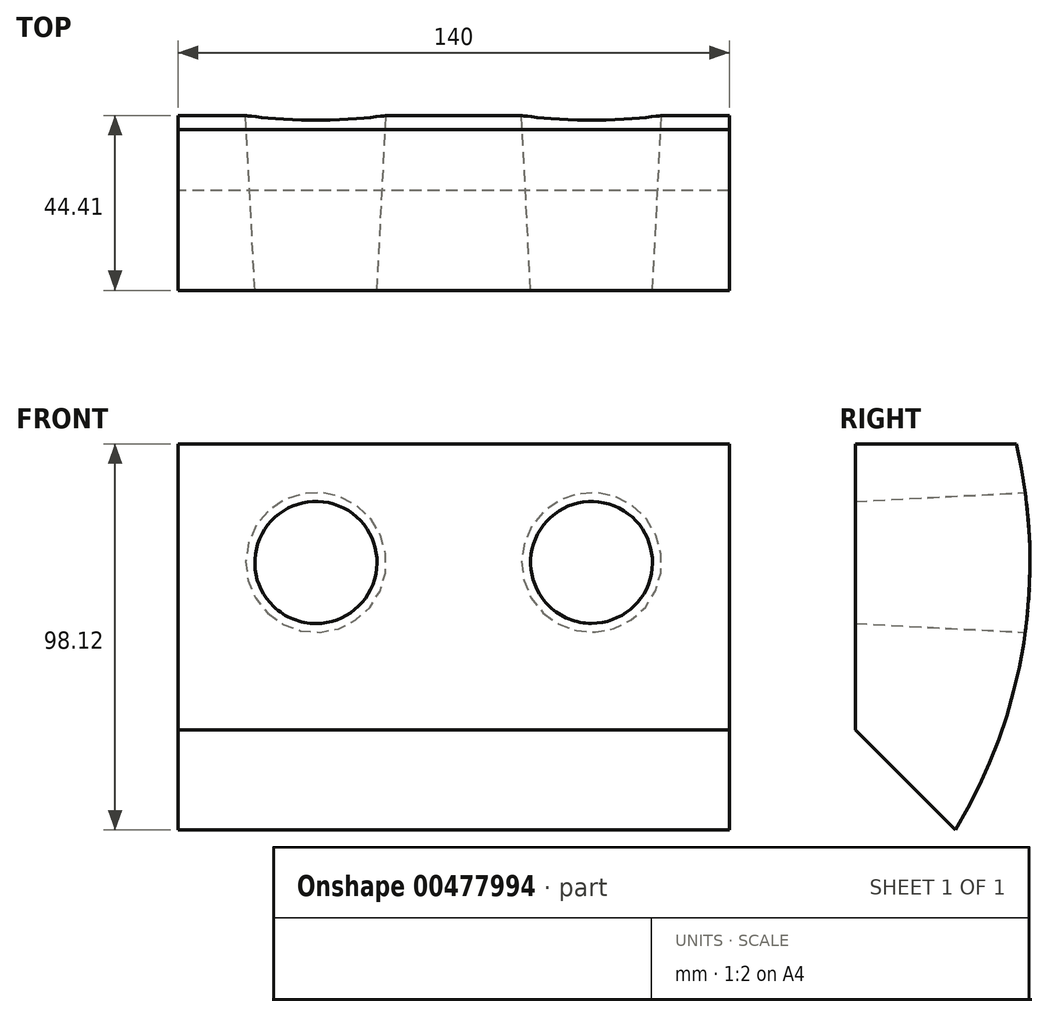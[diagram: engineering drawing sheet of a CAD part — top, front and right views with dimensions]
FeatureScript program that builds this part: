
annotation { "Feature Type Name" : "Feature", "Feature Type Description" : "" }
export const myFeature = defineFeature(function(context is Context, id is Id, definition is map)
    precondition{}
    {
        {
            var Q0;
            Q0=qCreatedBy(makeId("Right.planeOp"),FACE);
            cPlane(context, id + "F0", {"entities" : qUnion([Q0]), "cplaneType" : CPlaneType.OFFSET, "offset" : 70 * mm, "oppositeDirection" : true, "width" : 152.4 * mm, "height" : 152.4 * mm});
        }
        {
            var Q0;
            Q0=qCreatedBy(id+"F0.planeOp",FACE);
            var sketch = newSketch(context, id + "F1", { "sketchPlane" : qUnion([Q0])});
            skLineSegment(sketch, "E0", {"start": v(0, 0) * mm, "end": v(19.01, 0) * mm});
            skLineSegment(sketch, "E1", {"start": v(0, 0) * mm, "end": v(0, 67.98) * mm});
            skLineSegment(sketch, "E2", {"start": v(0, 0) * mm, "end": v(0, -67.97) * mm});
            skArc(sketch, "E3", {"start": v(0, -67.97) * mm, "mid": v(19.01, 0) * mm, "end": v(0, 67.98) * mm});
            skSolve(sketch);
        }
        {
            var Q0;
            {var subQ0=sQuery(id+"F1.wireOp",EDGE,"E0");Q0=makeQuery(id+"F1.imprint","IMPRINT",FACE,{"disambiguationData":[TD([[makeQuery(id+"F1.imprint","IMPRINT",EDGE,{"derivedFrom":subQ0}),1.0]])]});}
            var Q1;
            {var subQ0=sQuery(id+"F1.wireOp",EDGE,"E0");Q1=makeQuery(id+"F1.imprint","IMPRINT",FACE,{"disambiguationData":[TD([[makeQuery(id+"F1.imprint","IMPRINT",EDGE,{"derivedFrom":subQ0}),-1.0]])]});}
            var Q2;
            Q2 = qSketchRegion(id + "F1", true);
            extrude(context, id + "F2", {"entities" : qUnion([Q0, Q1, Q2]), "depth" : 140 * mm});
        }
        {
            var Q0;
            Q0=makeQuery(id+"F2.opExtrude","SWEPT_FACE",FACE,{"disambiguationData":[OSD([sQuery(id+"F1.wireOp",EDGE,"E1"),sQuery(id+"F1.wireOp",EDGE,"E2")])]});
            extrude(context, id + "F3", {"entities" : qUnion([Q0]), "operationType" : NewBodyOperationType.ADD, "depth" : 25.4 * mm});
        }
        {
            var Q0;
            Q0=makeQuery(id+"F3.opExtrude","CAP_FACE",FACE,{"disambiguationData":[OSD([sQuery(id+"F1.wireOp",EDGE,"E1"),sQuery(id+"F1.wireOp",EDGE,"E2")])],"isStart":false});
            var sketch = newSketch(context, id + "F4", { "sketchPlane" : qUnion([Q0])});
            skLineSegment(sketch, "E4", {"start": v(0, 0) * mm, "end": v(-35.01, 0) * mm});
            skLineSegment(sketch, "E5", {"start": v(0, 0) * mm, "end": v(35.01, 0) * mm});
            skSolve(sketch);
        }
        {
            var Q0;
            {var subQ0=sQuery(id+"F1.wireOp",EDGE,"E3");var subQ1=sQuery(id+"F1.wireOp",EDGE,"E1");Q0=makeQuery(id+"F4.imprint","IMPRINT",FACE,{"disambiguationData":[TD([[makeQuery(id+"F4.imprint","IMPRINT",EDGE,{"derivedFrom":makeQuery(id+"F3.opExtrude","CAP_EDGE",EDGE,{"disambiguationData":[OSD([subQ1,subQ0])],"isStart":false})}),1.0]])]});}
            var sketch = newSketch(context, id + "F5", { "sketchPlane" : qUnion([Q0])});
            skCircle(sketch, "E6", {"center": v(-35.02, 0) * mm, "radius": 15.52 * mm});
            skCircle(sketch, "E7", {"center": v(35, 0) * mm, "radius": 15.48 * mm});
            skLineSegment(sketch, "E8.bottom", {"start": v(-19.32, -15.87) * mm, "end": v(-50.71, -15.87) * mm});
            skLineSegment(sketch, "E8.top", {"start": v(-19.32, 15.87) * mm, "end": v(-50.71, 15.87) * mm});
            skLineSegment(sketch, "E8.left", {"start": v(-19.32, -15.87) * mm, "end": v(-19.32, 15.87) * mm});
            skLineSegment(sketch, "E8.right", {"start": v(-50.71, -15.87) * mm, "end": v(-50.71, 15.87) * mm});
            skLineSegment(sketch, "E9.bottom", {"start": v(50.7, -15.87) * mm, "end": v(19.32, -15.87) * mm});
            skLineSegment(sketch, "E9.top", {"start": v(50.7, 15.87) * mm, "end": v(19.32, 15.87) * mm});
            skLineSegment(sketch, "E9.left", {"start": v(50.7, -15.87) * mm, "end": v(50.7, 15.87) * mm});
            skLineSegment(sketch, "E9.right", {"start": v(19.32, -15.87) * mm, "end": v(19.32, 15.87) * mm});
            skSolve(sketch);
        }
        {
            var Q0;
            Q0=qCreatedBy(id+"F0.planeOp",FACE);
            var sketch = newSketch(context, id + "F6", { "sketchPlane" : qUnion([Q0])});
            skLineSegment(sketch, "E10.bottom", {"start": v(-80.1, 30.15) * mm, "end": v(135.05, 30.15) * mm});
            skLineSegment(sketch, "E10.top", {"start": v(-80.1, 114.47) * mm, "end": v(135.05, 114.47) * mm});
            skLineSegment(sketch, "E10.left", {"start": v(-80.1, 30.15) * mm, "end": v(-80.1, 114.47) * mm});
            skLineSegment(sketch, "E10.right", {"start": v(135.05, 30.15) * mm, "end": v(135.05, 114.47) * mm});
            skPoint(sketch, "E10.middle", {"position": v(27.47, 72.31) * mm});
            skSolve(sketch);
        }
        {
            var Q0;
            Q0=makeQuery(id+"F6.imprint","IMPRINT",FACE,{"disambiguationData":[TD([[makeQuery(id+"F6.imprint","IMPRINT",EDGE,{"derivedFrom":sQuery(id+"F6.wireOp",EDGE,"E10.bottom")}),1.0]])]});
            extrude(context, id + "F7", {"entities" : qUnion([Q0]), "operationType" : NewBodyOperationType.REMOVE, "endBound" : BoundingType.THROUGH_ALL, "depth" : 25.4 * mm});
        }
        {
            var Q0;
            {var subQ0=sQuery(id+"F1.wireOp",EDGE,"E2");var subQ1=sQuery(id+"F1.wireOp",EDGE,"E1");Q0=makeQuery(id+"F3.boolean.opBoolean","MERGE",FACE,{"derivedFrom":[makeQuery(id+"F2.opExtrude","CAP_FACE",FACE,{"disambiguationData":[OSD([subQ1,subQ0,sQuery(id+"F1.wireOp",EDGE,"E3")])],"isStart":true}),makeQuery(id+"F3.opExtrude","SWEPT_FACE",FACE,{"disambiguationData":[OSD([subQ1,subQ0]),TDD([makeQuery(id+"F2.opExtrude","CAP_EDGE",EDGE,{"disambiguationData":[OSD([subQ1,subQ0])],"isStart":true})])]})]});}
            var sketch = newSketch(context, id + "F8", { "sketchPlane" : qUnion([Q0])});
            skLineSegment(sketch, "E11", {"start": v(25.4, -67.97) * mm, "end": v(25.4, -42.57) * mm});
            skLineSegment(sketch, "E12", {"start": v(25.4, -42.57) * mm, "end": v(0, -67.97) * mm});
            skLineSegment(sketch, "E13", {"start": v(0, -67.97) * mm, "end": v(25.4, -67.97) * mm});
            skSolve(sketch);
        }
        {
            var Q0;
            Q0=makeQuery(id+"F8.imprint","IMPRINT",FACE,{"disambiguationData":[TD([[makeQuery(id+"F8.imprint","IMPRINT",EDGE,{"derivedFrom":sQuery(id+"F8.wireOp",EDGE,"E11")}),1.0]])]});
            extrude(context, id + "F9", {"entities" : qUnion([Q0]), "operationType" : NewBodyOperationType.REMOVE, "endBound" : BoundingType.THROUGH_ALL, "oppositeDirection" : true, "depth" : 25.4 * mm});
        }
        {
            var Q0;
            Q0=makeQuery(id+"F5.imprint","IMPRINT",FACE,{"disambiguationData":[TD([[makeQuery(id+"F5.imprint","IMPRINT",EDGE,{"derivedFrom":sQuery(id+"F5.wireOp",EDGE,"E6")}),1.0]])]});
            var Q1;
            Q1=makeQuery(id+"F5.imprint","IMPRINT",FACE,{"disambiguationData":[TD([[makeQuery(id+"F5.imprint","IMPRINT",EDGE,{"derivedFrom":sQuery(id+"F5.wireOp",EDGE,"E7")}),1.0]])]});
            var Q2;
            Q2=sQuery(id+"F5.wireOp",EDGE,"E6");
            var Q3;
            Q3=sQuery(id+"F5.wireOp",EDGE,"E7");
            extrude(context, id + "F10", {"entities" : qUnion([Q0, Q1]), "operationType" : NewBodyOperationType.REMOVE, "surfaceEntities" : qUnion([Q2, Q3]), "endBound" : BoundingType.THROUGH_ALL, "oppositeDirection" : true, "depth" : 101.6 * mm, "hasDraft" : true, "draftAngle" : 3 * degree});
        }
    });
